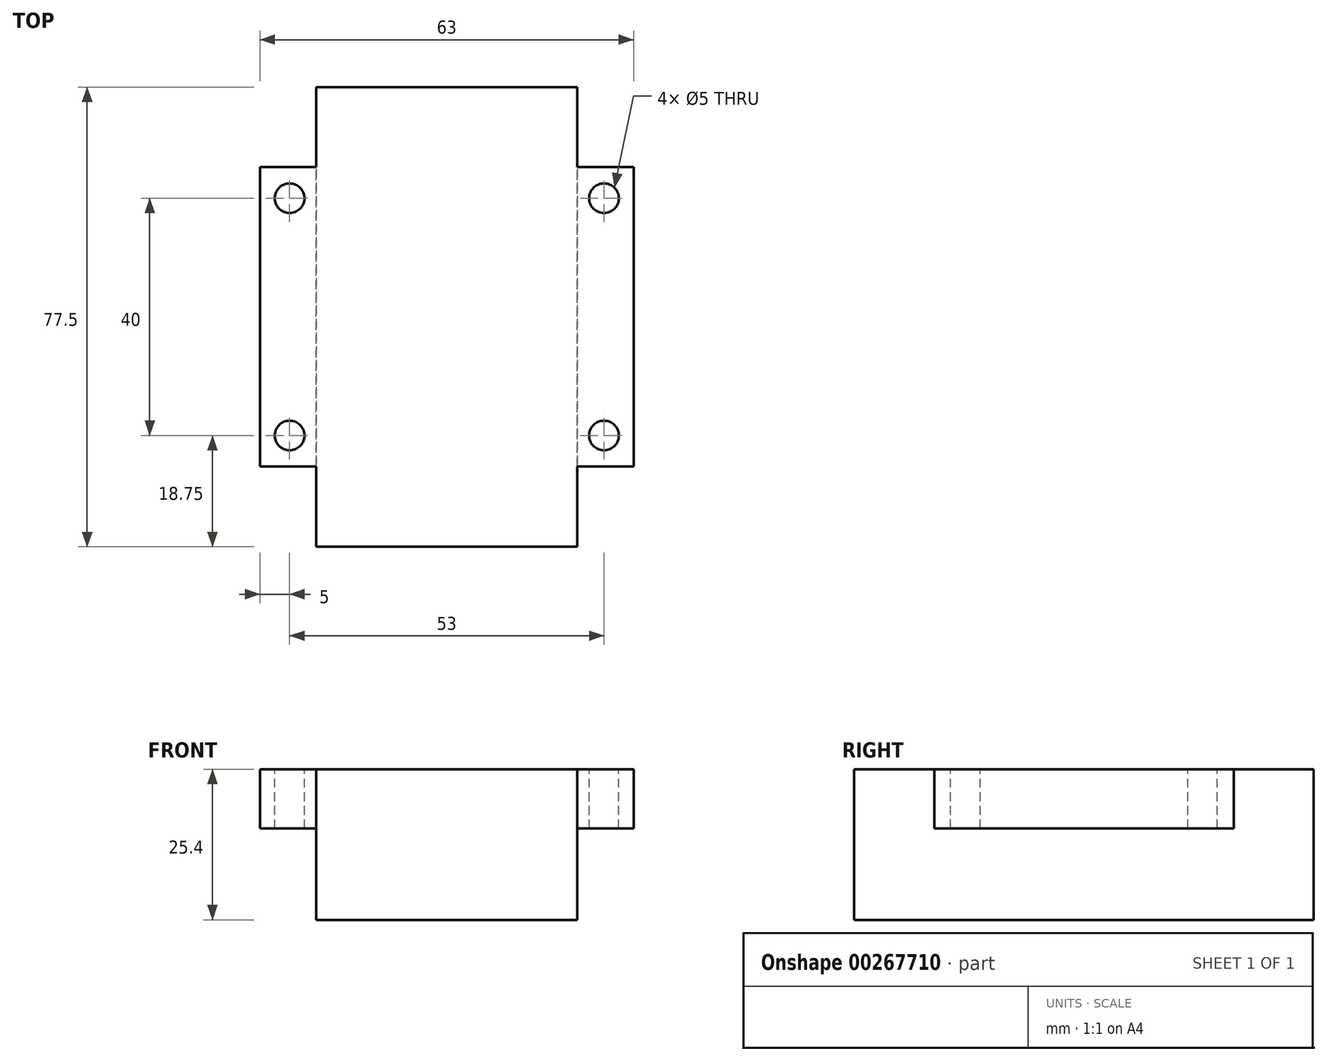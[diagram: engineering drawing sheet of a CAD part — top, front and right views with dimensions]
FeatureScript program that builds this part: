
annotation { "Feature Type Name" : "Feature", "Feature Type Description" : "" }
export const myFeature = defineFeature(function(context is Context, id is Id, definition is map)
    precondition{}
    {
        {
            var Q0;
            Q0=qCreatedBy(makeId("Front.planeOp"),FACE);
            var sketch = newSketch(context, id + "F0", { "sketchPlane" : qUnion([Q0])});
            skLineSegment(sketch, "E0.bottom", {"start": v(-22, 12.7) * mm, "end": v(22, 12.7) * mm});
            skLineSegment(sketch, "E0.top", {"start": v(-22, -12.7) * mm, "end": v(22, -12.7) * mm});
            skLineSegment(sketch, "E0.left", {"start": v(-22, 12.7) * mm, "end": v(-22, -12.7) * mm});
            skLineSegment(sketch, "E0.right", {"start": v(22, 12.7) * mm, "end": v(22, -12.7) * mm});
            skPoint(sketch, "E0.middle", {"position": v(0, 0) * mm});
            skSolve(sketch);
        }
        {
            var Q0;
            Q0=qSketchRegion(id+"F0",true);
            extrude(context, id + "F1", {"entities" : qUnion([Q0]), "oppositeDirection" : true, "depth" : 77.5 * mm});
        }
        {
            var Q0;
            Q0=makeQuery(id+"F1.opExtrude","SWEPT_FACE",FACE,{"disambiguationData":[OSD([sQuery(id+"F0.wireOp",EDGE,"E0.bottom")])]});
            var sketch = newSketch(context, id + "F2", { "sketchPlane" : qUnion([Q0])});
            skLineSegment(sketch, "E1.bottom", {"start": v(16, 118.22) * mm, "end": v(-16, 118.22) * mm, "construction": true});
            skLineSegment(sketch, "E1.top", {"start": v(16, -118.22) * mm, "end": v(-16, -118.22) * mm, "construction": true});
            skLineSegment(sketch, "E1.left", {"start": v(16, 118.22) * mm, "end": v(16, -118.22) * mm, "construction": true});
            skLineSegment(sketch, "E1.right", {"start": v(-16, 118.22) * mm, "end": v(-16, -118.22) * mm, "construction": true});
            skPoint(sketch, "E1.middle", {"position": v(0, 0) * mm});
            skLineSegment(sketch, "E2", {"start": v(-22, 38.75) * mm, "end": v(22, 38.75) * mm, "construction": true});
            skLineSegment(sketch, "E3.bottom", {"start": v(16, 56.75) * mm, "end": v(-25.34, 56.75) * mm, "construction": true});
            skLineSegment(sketch, "E3.top", {"start": v(16, 20.75) * mm, "end": v(-25.34, 20.75) * mm, "construction": true});
            skLineSegment(sketch, "E3.right", {"start": v(-25.34, 56.75) * mm, "end": v(-25.34, 20.75) * mm, "construction": true});
            skPoint(sketch, "E3.middle", {"position": v(-4.67, 38.75) * mm});
            skSolve(sketch);
        }
        {
            var Q0;
            Q0=makeQuery(id+"F1.opExtrude","SWEPT_FACE",FACE,{"disambiguationData":[OSD([sQuery(id+"F0.wireOp",EDGE,"E0.bottom")])]});
            var sketch = newSketch(context, id + "F3", { "sketchPlane" : qUnion([Q0])});
            skLineSegment(sketch, "E4.bottom", {"start": v(31.5, 64) * mm, "end": v(-31.5, 64) * mm});
            skLineSegment(sketch, "E4.top", {"start": v(31.5, 13.5) * mm, "end": v(-31.5, 13.5) * mm});
            skLineSegment(sketch, "E4.left", {"start": v(31.5, 64) * mm, "end": v(31.5, 13.5) * mm});
            skLineSegment(sketch, "E4.right", {"start": v(-31.5, 64) * mm, "end": v(-31.5, 13.5) * mm});
            skPoint(sketch, "E4.middle", {"position": v(0, 38.75) * mm});
            skLineSegment(sketch, "E5", {"start": v(0, 64) * mm, "end": v(-26.5, 64) * mm, "construction": true});
            skLineSegment(sketch, "E6", {"start": v(0, 64) * mm, "end": v(26.5, 64) * mm, "construction": true});
            skLineSegment(sketch, "E7", {"start": v(-26.5, 64) * mm, "end": v(-26.5, 13.5) * mm, "construction": true});
            skLineSegment(sketch, "E8", {"start": v(26.5, 64) * mm, "end": v(26.5, 13.5) * mm, "construction": true});
            skLineSegment(sketch, "E9", {"start": v(0, 38.75) * mm, "end": v(0, 58.75) * mm, "construction": true});
            skLineSegment(sketch, "E10", {"start": v(0, 38.75) * mm, "end": v(0, 18.75) * mm, "construction": true});
            skLineSegment(sketch, "E11", {"start": v(0, 58.75) * mm, "end": v(-26.5, 58.75) * mm, "construction": true});
            skLineSegment(sketch, "E12", {"start": v(-26.5, 58.75) * mm, "end": v(-26.5, 18.75) * mm, "construction": true});
            skCircle(sketch, "E13", {"center": v(-26.5, 58.75) * mm, "radius": 2.5 * mm});
            skCircle(sketch, "E14", {"center": v(-26.5, 18.75) * mm, "radius": 2.5 * mm});
            skCircle(sketch, "E15", {"center": v(26.5, 18.75) * mm, "radius": 2.5 * mm});
            skCircle(sketch, "E16", {"center": v(26.5, 58.75) * mm, "radius": 2.5 * mm});
            skPoint(sketch, "E16.centerSnap0", {"position": v(-13.25, 58.75) * mm});
            skSolve(sketch);
        }
        {
            var Q0;
            Q0 = qSketchRegion(id + "F3", true);
            var Q1;
            {var subQ0=sQuery(id+"F0.wireOp",EDGE,"E0.bottom");Q1=makeQuery(id+"F2.imprint","IMPRINT",FACE,{"disambiguationData":[TD([[makeQuery(id+"F2.imprint","IMPRINT",EDGE,{"derivedFrom":makeQuery(id+"F1.opExtrude","CAP_EDGE",EDGE,{"disambiguationData":[OSD([subQ0])],"isStart":true})}),1.0]])]});}
            extrude(context, id + "F4", {"entities" : qUnion([Q0, Q1]), "operationType" : NewBodyOperationType.ADD, "oppositeDirection" : true, "depth" : 10 * mm});
        }
    });
